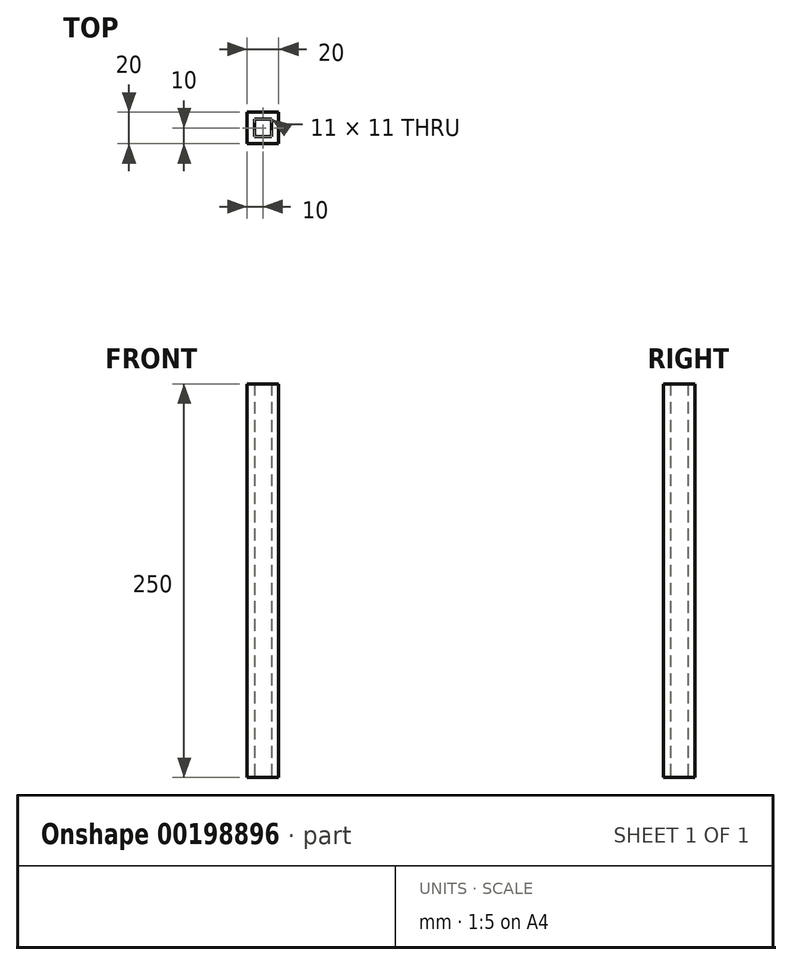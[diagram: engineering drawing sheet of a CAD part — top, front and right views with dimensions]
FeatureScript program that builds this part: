
annotation { "Feature Type Name" : "Feature", "Feature Type Description" : "" }
export const myFeature = defineFeature(function(context is Context, id is Id, definition is map)
    precondition{}
    {
        {
            var Q0;
            Q0=qCreatedBy(makeId("Top.planeOp"),FACE);
            var sketch = newSketch(context, id + "F0", { "sketchPlane" : qUnion([Q0])});
            skLineSegment(sketch, "E0.bottom", {"start": v(10, 10) * mm, "end": v(-10, 10) * mm});
            skLineSegment(sketch, "E0.top", {"start": v(10, -10) * mm, "end": v(-10, -10) * mm});
            skLineSegment(sketch, "E0.left", {"start": v(10, 10) * mm, "end": v(10, -10) * mm});
            skLineSegment(sketch, "E0.right", {"start": v(-10, 10) * mm, "end": v(-10, -10) * mm});
            skPoint(sketch, "E0.middle", {"position": v(0, 0) * mm});
            skLineSegment(sketch, "E1.bottom", {"start": v(5.5, 5.5) * mm, "end": v(-5.5, 5.5) * mm});
            skLineSegment(sketch, "E1.top", {"start": v(5.5, -5.5) * mm, "end": v(-5.5, -5.5) * mm});
            skLineSegment(sketch, "E1.left", {"start": v(5.5, 5.5) * mm, "end": v(5.5, -5.5) * mm});
            skLineSegment(sketch, "E1.right", {"start": v(-5.5, 5.5) * mm, "end": v(-5.5, -5.5) * mm});
            skSolve(sketch);
        }
        {
            var Q0;
            Q0=makeQuery(id+"F0.imprint","IMPRINT",FACE,{"disambiguationData":[TD([[makeQuery(id+"F0.imprint","IMPRINT",EDGE,{"derivedFrom":sQuery(id+"F0.wireOp",EDGE,"E0.bottom")}),1.0]])]});
            extrude(context, id + "F1", {"entities" : qUnion([Q0]), "depth" : 250 * mm});
        }
    });
